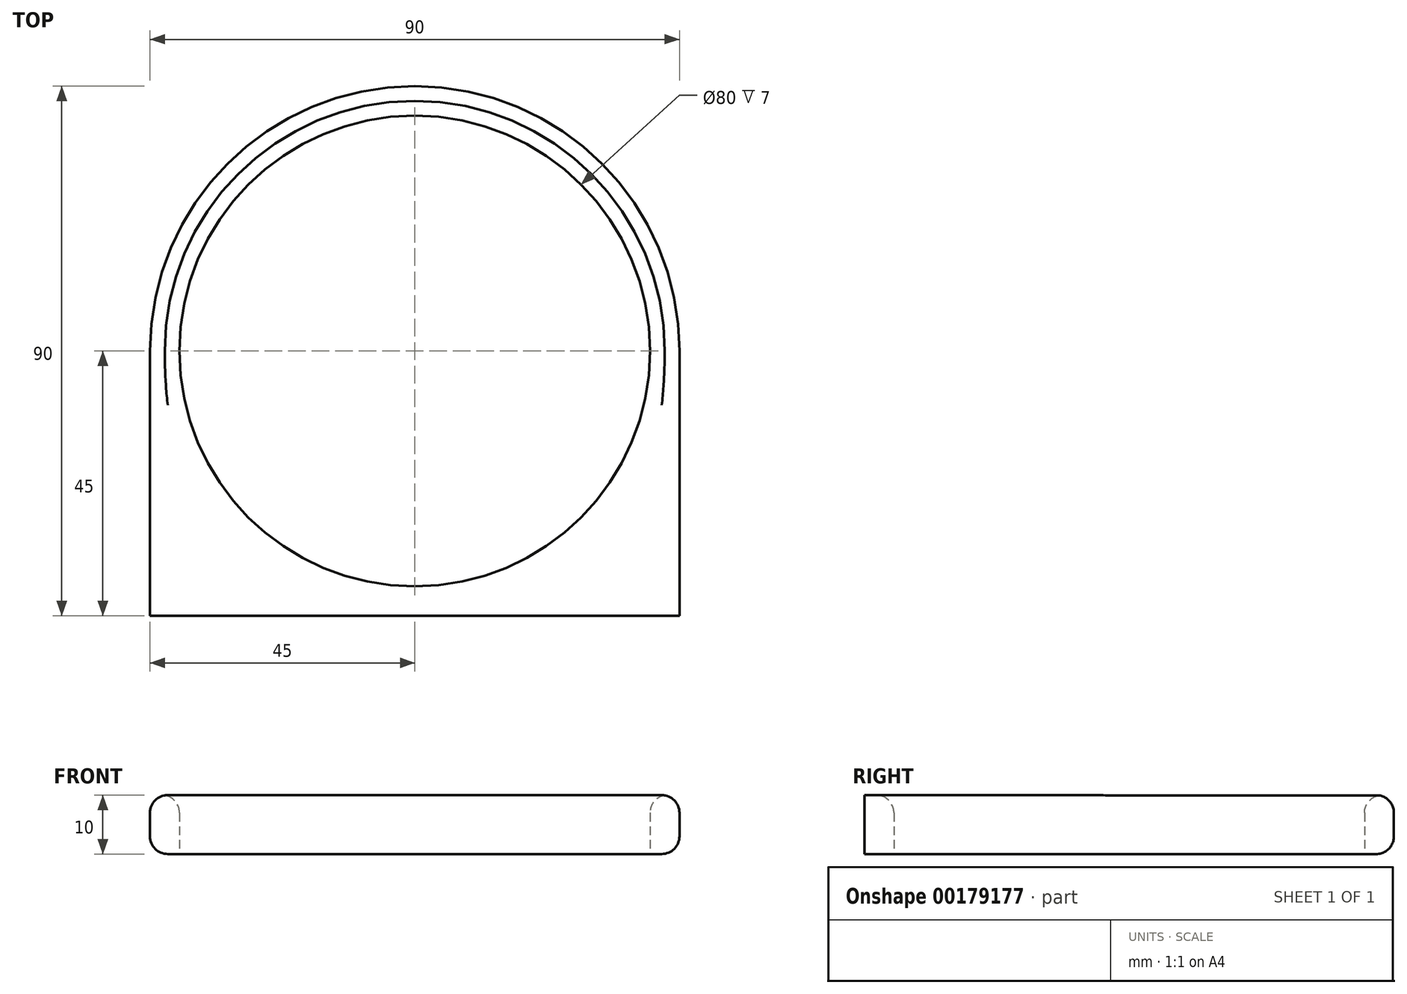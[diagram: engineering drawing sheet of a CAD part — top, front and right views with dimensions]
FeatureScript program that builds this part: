
annotation { "Feature Type Name" : "Feature", "Feature Type Description" : "" }
export const myFeature = defineFeature(function(context is Context, id is Id, definition is map)
    precondition{}
    {
        {
            var Q0;
            Q0=qCreatedBy(makeId("Top.planeOp"),FACE);
            var sketch = newSketch(context, id + "F0", { "sketchPlane" : qUnion([Q0])});
            skArc(sketch, "E0", {"start": v(0, -40) * mm, "mid": v(40, 0) * mm, "end": v(0, 40) * mm});
            skLineSegment(sketch, "E1", {"start": v(0, 57.66) * mm, "end": v(0, -61.56) * mm, "construction": true});
            skLineSegment(sketch, "E2", {"start": v(45, 0) * mm, "end": v(45, -45) * mm});
            skLineSegment(sketch, "E3", {"start": v(45, -45) * mm, "end": v(0, -45) * mm});
            skArc(sketch, "E4.MirrorCS", {"start": v(0, -40) * mm, "mid": v(-40, 0) * mm, "end": v(0, 40) * mm});
            skLineSegment(sketch, "E5.MirrorCS", {"start": v(-45, 0) * mm, "end": v(-45, -45) * mm});
            skLineSegment(sketch, "E6.MirrorCS", {"start": v(-45, -45) * mm, "end": v(0, -45) * mm});
            skArc(sketch, "E7", {"start": v(-45, 0) * mm, "mid": v(0, 45) * mm, "end": v(45, 0) * mm});
            skSolve(sketch);
        }
        {
            var Q0;
            Q0=makeQuery(id+"F0.imprint","IMPRINT",FACE,{"disambiguationData":[TD([[makeQuery(id+"F0.imprint","IMPRINT",EDGE,{"derivedFrom":sQuery(id+"F0.wireOp",EDGE,"E0")}),-1.0]])]});
            extrude(context, id + "F1", {"entities" : qUnion([Q0]), "depth" : 10 * mm});
        }
        {
            var Q0;
            Q0=makeQuery(id+"F1.opExtrude","CAP_EDGE",EDGE,{"disambiguationData":[OSD([sQuery(id+"F0.wireOp",EDGE,"E0"),sQuery(id+"F0.wireOp",EDGE,"E4.MirrorCS")])],"isStart":false});
            var Q1;
            Q1=makeQuery(id+"F1.opExtrude","CAP_EDGE",EDGE,{"disambiguationData":[OSD([sQuery(id+"F0.wireOp",EDGE,"E5.MirrorCS")])],"isStart":false});
            var Q2;
            Q2=makeQuery(id+"F1.opExtrude","CAP_EDGE",EDGE,{"disambiguationData":[OSD([sQuery(id+"F0.wireOp",EDGE,"E7")])],"isStart":false});
            var Q3;
            Q3=makeQuery(id+"F1.opExtrude","CAP_EDGE",EDGE,{"disambiguationData":[OSD([sQuery(id+"F0.wireOp",EDGE,"E5.MirrorCS")])],"isStart":true});
            var Q4;
            Q4=makeQuery(id+"F1.opExtrude","CAP_EDGE",EDGE,{"disambiguationData":[OSD([sQuery(id+"F0.wireOp",EDGE,"E2")])],"isStart":true});
            var Q5;
            Q5=makeQuery(id+"F1.opExtrude","CAP_EDGE",EDGE,{"disambiguationData":[OSD([sQuery(id+"F0.wireOp",EDGE,"E7")])],"isStart":true});
            fillet(context, id + "F2", {"entities" : qUnion([Q0, Q1, Q2, Q3, Q4, Q5]), "radius" : 3 * mm, "tangentPropagation" : true, "allowEdgeOverflow" : false});
        }
    });
